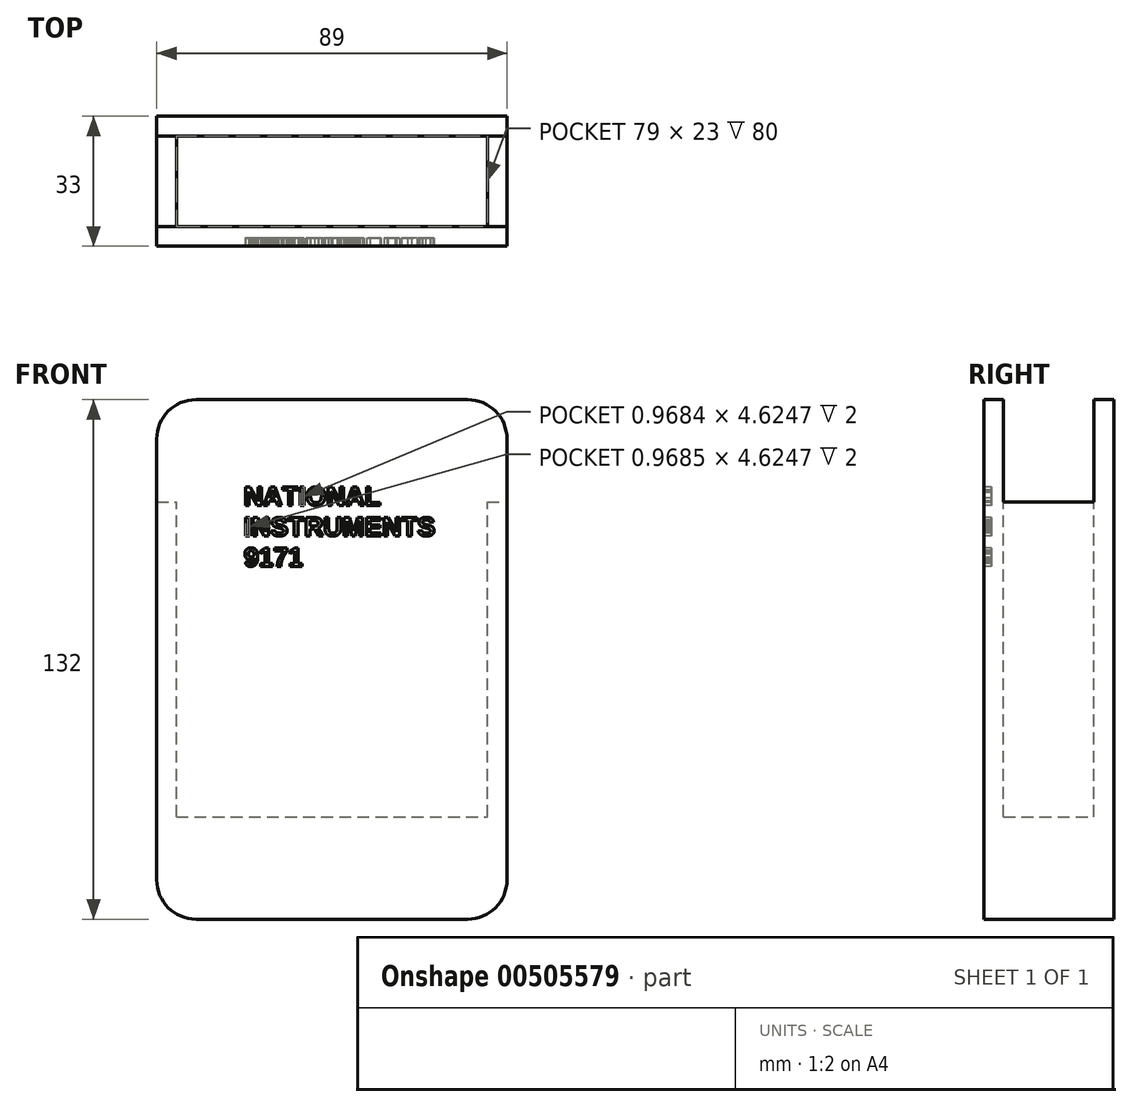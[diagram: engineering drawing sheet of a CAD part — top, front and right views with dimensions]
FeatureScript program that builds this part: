
annotation { "Feature Type Name" : "Feature", "Feature Type Description" : "" }
export const myFeature = defineFeature(function(context is Context, id is Id, definition is map)
    precondition{}
    {
        {
            var Q0;
            Q0=qCreatedBy(makeId("Front.planeOp"),FACE);
            var sketch = newSketch(context, id + "F0", { "sketchPlane" : qUnion([Q0])});
            skLineSegment(sketch, "E0.bottom", {"start": v(0, 0) * mm, "end": v(89, 0) * mm});
            skLineSegment(sketch, "E0.top", {"start": v(0, 132) * mm, "end": v(89, 132) * mm});
            skLineSegment(sketch, "E0.left", {"start": v(0, 0) * mm, "end": v(0, 132) * mm});
            skLineSegment(sketch, "E0.right", {"start": v(89, 0) * mm, "end": v(89, 132) * mm});
            skSolve(sketch);
        }
        {
            var Q0;
            Q0 = qSketchRegion(id + "F0", true);
            extrude(context, id + "F1", {"entities" : qUnion([Q0]), "depth" : 33 * mm});
        }
        {
            var Q0;
            Q0=makeQuery(id+"F1.opExtrude","SWEPT_EDGE",EDGE,{"disambiguationData":[OSD([sQuery(id+"F0.wireOp",EDGE,"E0.top"),sQuery(id+"F0.wireOp",EDGE,"E0.left")])]});
            var Q1;
            Q1=makeQuery(id+"F1.opExtrude","SWEPT_EDGE",EDGE,{"disambiguationData":[OSD([sQuery(id+"F0.wireOp",EDGE,"E0.top"),sQuery(id+"F0.wireOp",EDGE,"E0.right")])]});
            var Q2;
            Q2=makeQuery(id+"F1.opExtrude","SWEPT_EDGE",EDGE,{"disambiguationData":[OSD([sQuery(id+"F0.wireOp",EDGE,"E0.bottom"),sQuery(id+"F0.wireOp",EDGE,"E0.right")])]});
            var Q3;
            Q3=makeQuery(id+"F1.opExtrude","SWEPT_EDGE",EDGE,{"disambiguationData":[OSD([sQuery(id+"F0.wireOp",EDGE,"E0.bottom"),sQuery(id+"F0.wireOp",EDGE,"E0.left")])]});
            fillet(context, id + "F2", {"entities" : qUnion([Q0, Q1, Q2, Q3]), "radius" : 10 * mm, "tangentPropagation" : true, "allowEdgeOverflow" : false});
        }
        {
            var Q0;
            Q0=makeQuery(id+"F1.opExtrude","CAP_FACE",FACE,{"disambiguationData":[OSD([sQuery(id+"F0.wireOp",EDGE,"E0.bottom"),sQuery(id+"F0.wireOp",EDGE,"E0.top"),sQuery(id+"F0.wireOp",EDGE,"E0.left"),sQuery(id+"F0.wireOp",EDGE,"E0.right")])],"isStart":false});
            var sketch = newSketch(context, id + "F3", { "sketchPlane" : qUnion([Q0])});
            skText(sketch, "E1", { "text": "NATIONAL\nINSTRUMENTS\n9171", "fontName": "Arimo-Bold.ttf"});
            const initialGuessF3  = {"E1": [0.02218, 0.10514, 1, 0, 0.00484]};
            skSetInitialGuess(sketch, initialGuessF3);
            skSolve(sketch);
        }
        {
            var Q0;
            Q0 = qSketchRegion(id + "F3", true);
            extrude(context, id + "F4", {"entities" : qUnion([Q0]), "operationType" : NewBodyOperationType.REMOVE, "oppositeDirection" : true, "depth" : 2 * mm});
        }
        {
            var Q0;
            Q0=makeQuery(id+"F1.opExtrude","SWEPT_FACE",FACE,{"disambiguationData":[OSD([sQuery(id+"F0.wireOp",EDGE,"E0.right")])]});
            var sketch = newSketch(context, id + "F5", { "sketchPlane" : qUnion([Q0])});
            skLineSegment(sketch, "E2", {"start": v(-16.5, 106) * mm, "end": v(-5, 106) * mm});
            skLineSegment(sketch, "E3", {"start": v(-16.5, 106) * mm, "end": v(-28, 106) * mm});
            skLineSegment(sketch, "E4", {"start": v(-28, 106) * mm, "end": v(-28, 138) * mm});
            skLineSegment(sketch, "E5", {"start": v(-28, 138) * mm, "end": v(-5, 138) * mm});
            skLineSegment(sketch, "E6", {"start": v(-5, 138) * mm, "end": v(-5, 106) * mm});
            skSolve(sketch);
        }
        {
            var Q0;
            Q0 = qSketchRegion(id + "F5", true);
            extrude(context, id + "F6", {"entities" : qUnion([Q0]), "operationType" : NewBodyOperationType.REMOVE, "endBound" : BoundingType.THROUGH_ALL, "oppositeDirection" : true, "depth" : 25 * mm});
        }
        {
            var Q0;
            Q0=makeQuery(id+"F6.boolean.opBoolean","COPY",FACE,{"derivedFrom":makeQuery(id+"F6.opExtrude","SWEPT_FACE",FACE,{"disambiguationData":[OSD([sQuery(id+"F5.wireOp",EDGE,"E2"),sQuery(id+"F5.wireOp",EDGE,"E3")])]})});
            var sketch = newSketch(context, id + "F7", { "sketchPlane" : qUnion([Q0])});
            skLineSegment(sketch, "E7.0", {"start": v(5, -28) * mm, "end": v(5, -5) * mm});
            skLineSegment(sketch, "E8.0", {"start": v(84, -5) * mm, "end": v(84, -28) * mm});
            skLineSegment(sketch, "E9", {"start": v(5, -5) * mm, "end": v(84, -5) * mm});
            skLineSegment(sketch, "E10", {"start": v(5, -28) * mm, "end": v(84, -28) * mm});
            skSolve(sketch);
        }
        {
            var Q0;
            Q0 = qSketchRegion(id + "F7", true);
            extrude(context, id + "F8", {"entities" : qUnion([Q0]), "operationType" : NewBodyOperationType.REMOVE, "oppositeDirection" : true, "depth" : 80 * mm});
        }
    });
